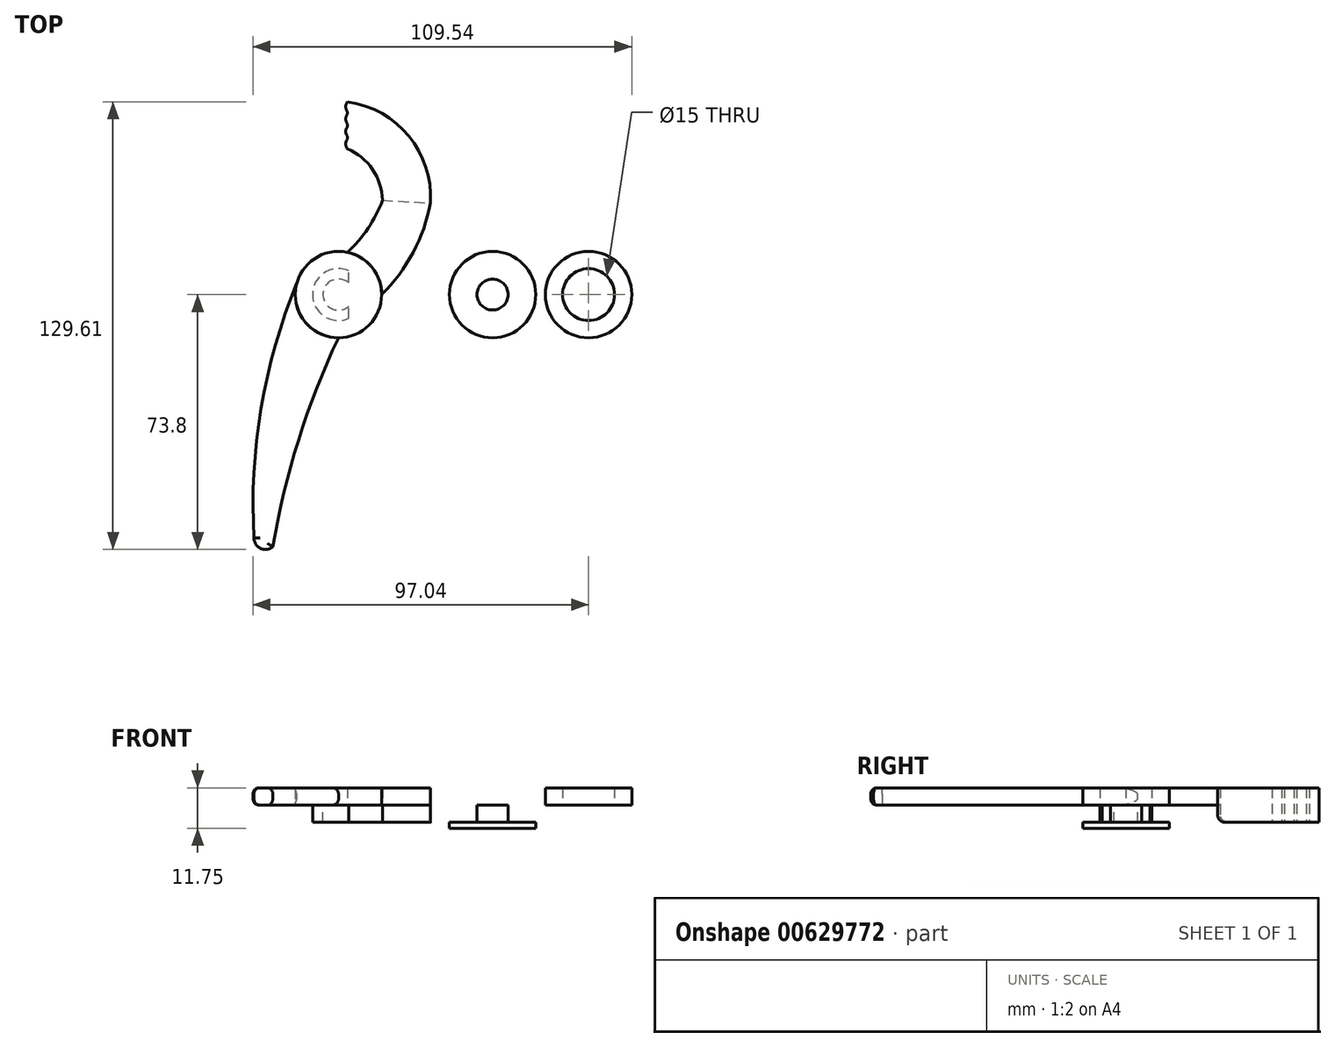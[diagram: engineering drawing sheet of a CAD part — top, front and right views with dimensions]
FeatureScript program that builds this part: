
annotation { "Feature Type Name" : "Feature", "Feature Type Description" : "" }
export const myFeature = defineFeature(function(context is Context, id is Id, definition is map)
    precondition{}
    {
        {
            var Q0;
            Q0=qCreatedBy(makeId("Top.planeOp"),FACE);
            var sketch = newSketch(context, id + "F0", { "sketchPlane" : qUnion([Q0])});
            skCircle(sketch, "E0", {"center": v(0, 0) * mm, "radius": 12.5 * mm});
            skArc(sketch, "E1", {"start": v(0, -12.5) * mm, "mid": v(-11.56, -42.1) * mm, "end": v(-19, -73) * mm});
            skArc(sketch, "E2", {"start": v(-24.43, -70.5) * mm, "mid": v(-22.51, -73.5) * mm, "end": v(-19, -73) * mm});
            skArc(sketch, "E3", {"start": v(-12.08, 3.22) * mm, "mid": v(-22.4, -32.95) * mm, "end": v(-24.43, -70.5) * mm});
            skArc(sketch, "E4", {"start": v(2.57, 12.23) * mm, "mid": v(8.53, 19.17) * mm, "end": v(12.73, 27.3) * mm});
            skArc(sketch, "E5", {"start": v(12.73, 27.3) * mm, "mid": v(9.86, 36.23) * mm, "end": v(2.65, 42.22) * mm});
            skLineSegment(sketch, "E6", {"start": v(2.65, 42.22) * mm, "end": v(2.65, 55.8) * mm});
            skArc(sketch, "E7", {"start": v(26.6, 26.5) * mm, "mid": v(20.35, 45.84) * mm, "end": v(2.65, 55.8) * mm});
            skArc(sketch, "E8", {"start": v(12.5, 0) * mm, "mid": v(21.58, 12.17) * mm, "end": v(26.6, 26.5) * mm});
            skLineSegment(sketch, "E9", {"start": v(12.73, 27.3) * mm, "end": v(26.6, 26.5) * mm});
            skSolve(sketch);
        }
        {
            var Q0;
            {var subQ0=sQuery(id+"F0.wireOp",EDGE,"E0");var subQ6=makeQuery(id+"F0.imprint","INTERSECT",VERTEX,{"derivedFrom":[subQ0,sQuery(id+"F0.wireOp",EDGE,"E4")]});Q0=makeQuery(id+"F0.imprint","IMPRINT",FACE,{"disambiguationData":[TD([[makeQuery(id+"F0.imprint","IMPRINT",EDGE,{"disambiguationData":[TD([[subQ6,1.0]])],"derivedFrom":subQ0}),1.0]])]});}
            extrude(context, id + "F1", {"entities" : qUnion([Q0]), "depth" : 5 * mm});
        }
        {
            var Q0;
            {var subQ0=sQuery(id+"F0.wireOp",EDGE,"E1");Q0=makeQuery(id+"F0.imprint","IMPRINT",FACE,{"disambiguationData":[TD([[makeQuery(id+"F0.imprint","IMPRINT",EDGE,{"derivedFrom":subQ0}),-1.0]])]});}
            var Q1;
            Q1=makeQuery(id+"F1.opExtrude","CAP_FACE",FACE,{"disambiguationData":[OSD([sQuery(id+"F0.wireOp",EDGE,"E0"),sQuery(id+"F0.wireOp",EDGE,"E3")])],"isStart":false});
            extrude(context, id + "F2", {"entities" : qUnion([Q0]), "endBound" : BoundingType.UP_TO_SURFACE, "endBoundEntityFace" : qUnion([Q1]), "depth" : 25 * mm});
        }
        {
            var Q0;
            {var subQ0=sQuery(id+"F0.wireOp",EDGE,"E4");Q0=makeQuery(id+"F0.imprint","IMPRINT",FACE,{"disambiguationData":[TD([[makeQuery(id+"F0.imprint","IMPRINT",EDGE,{"derivedFrom":subQ0}),-1.0]])]});}
            var Q1;
            Q1=makeQuery(id+"F1.opExtrude","CAP_FACE",FACE,{"disambiguationData":[OSD([sQuery(id+"F0.wireOp",EDGE,"E0"),sQuery(id+"F0.wireOp",EDGE,"E3")])],"isStart":false});
            extrude(context, id + "F3", {"entities" : qUnion([Q0]), "endBound" : BoundingType.UP_TO_SURFACE, "endBoundEntityFace" : qUnion([Q1]), "depth" : 25 * mm});
        }
        {
            var Q0;
            Q0=makeQuery(id+"F0.imprint","IMPRINT",FACE,{"disambiguationData":[TD([[makeQuery(id+"F0.imprint","IMPRINT",EDGE,{"derivedFrom":sQuery(id+"F0.wireOp",EDGE,"E5")}),-1.0]])]});
            var Q1;
            Q1=makeQuery(id+"F3.opExtrude","CAP_FACE",FACE,{"disambiguationData":[OSD([sQuery(id+"F0.wireOp",EDGE,"E0"),sQuery(id+"F0.wireOp",EDGE,"E4"),sQuery(id+"F0.wireOp",EDGE,"E8"),sQuery(id+"F0.wireOp",EDGE,"E9")])],"isStart":false});
            extrude(context, id + "F4", {"entities" : qUnion([Q0]), "operationType" : NewBodyOperationType.ADD, "endBound" : BoundingType.UP_TO_SURFACE, "endBoundEntityFace" : qUnion([Q1]), "depth" : 25 * mm, "hasSecondDirection" : true, "secondDirectionOppositeDirection" : true, "secondDirectionDepth" : 5 * mm});
        }
        {
            var Q0;
            Q0=qCreatedBy(makeId("Top.planeOp"),FACE);
            var sketch = newSketch(context, id + "F5", { "sketchPlane" : qUnion([Q0])});
            skCircle(sketch, "E10", {"center": v(0, 0) * mm, "radius": 7.5 * mm});
            skCircle(sketch, "E11.0", {"center": v(0, 0) * mm, "radius": 4.5 * mm});
            skLineSegment(sketch, "E12", {"start": v(0, 0) * mm, "end": v(0, 7.5) * mm});
            skLineSegment(sketch, "E13", {"start": v(-2.94, -6.9) * mm, "end": v(2.94, -6.9) * mm});
            skLineSegment(sketch, "E14", {"start": v(2.94, -6.9) * mm, "end": v(2.94, 6.9) * mm});
            skLineSegment(sketch, "E15", {"start": v(2.94, 6.9) * mm, "end": v(-2.94, 6.9) * mm});
            skLineSegment(sketch, "E16", {"start": v(-2.94, 6.9) * mm, "end": v(-2.94, -6.9) * mm});
            skSolve(sketch);
        }
        {
            var Q0;
            {var subQ0=sQuery(id+"F5.wireOp",EDGE,"E16");var subQ4=sQuery(id+"F5.wireOp",EDGE,"E11.0");var subQ5=makeQuery(id+"F5.imprint","INTERSECT",VERTEX,{"disambiguationData":[OD(0.0)],"derivedFrom":[subQ4,subQ0]});Q0=makeQuery(id+"F5.imprint","IMPRINT",FACE,{"disambiguationData":[TD([[makeQuery(id+"F5.imprint","IMPRINT",EDGE,{"disambiguationData":[TD([[subQ5,-1.0]])],"derivedFrom":subQ4}),-1.0]])]});}
            var Q1;
            {var subQ0=sQuery(id+"F5.wireOp",EDGE,"E14");var subQ4=sQuery(id+"F5.wireOp",EDGE,"E11.0");var subQ5=makeQuery(id+"F5.imprint","INTERSECT",VERTEX,{"disambiguationData":[OD(0.0)],"derivedFrom":[subQ4,subQ0]});Q1=makeQuery(id+"F5.imprint","IMPRINT",FACE,{"disambiguationData":[TD([[makeQuery(id+"F5.imprint","IMPRINT",EDGE,{"disambiguationData":[TD([[subQ5,1.0]])],"derivedFrom":subQ4}),-1.0]])]});}
            var Q2;
            {var subQ5=sQuery(id+"F5.wireOp",EDGE,"E13");Q2=makeQuery(id+"F5.imprint","IMPRINT",FACE,{"disambiguationData":[TD([[makeQuery(id+"F5.imprint","IMPRINT",EDGE,{"derivedFrom":subQ5}),1.0]])]});}
            var Q3;
            {var subQ0=sQuery(id+"F5.wireOp",EDGE,"E13");Q3=makeQuery(id+"F5.imprint","IMPRINT",FACE,{"disambiguationData":[TD([[makeQuery(id+"F5.imprint","IMPRINT",EDGE,{"derivedFrom":subQ0}),-1.0]])]});}
            var Q4;
            {var subQ0=sQuery(id+"F5.wireOp",EDGE,"E12");var subQ1=sQuery(id+"F5.wireOp",EDGE,"E11.0");var subQ2=makeQuery(id+"F5.imprint","INTERSECT",VERTEX,{"derivedFrom":[subQ1,subQ0]});Q4=makeQuery(id+"F5.imprint","IMPRINT",FACE,{"disambiguationData":[TD([[makeQuery(id+"F5.imprint","IMPRINT",EDGE,{"disambiguationData":[TD([[subQ2,-1.0]])],"derivedFrom":subQ1}),-1.0]])]});}
            var Q5;
            {var subQ0=sQuery(id+"F5.wireOp",EDGE,"E12");var subQ1=sQuery(id+"F5.wireOp",EDGE,"E11.0");var subQ2=makeQuery(id+"F5.imprint","INTERSECT",VERTEX,{"derivedFrom":[subQ1,subQ0]});Q5=makeQuery(id+"F5.imprint","IMPRINT",FACE,{"disambiguationData":[TD([[makeQuery(id+"F5.imprint","IMPRINT",EDGE,{"disambiguationData":[TD([[subQ2,1.0]])],"derivedFrom":subQ1}),-1.0]])]});}
            var Q6;
            {var subQ0=sQuery(id+"F5.wireOp",EDGE,"E12");var subQ1=sQuery(id+"F5.wireOp",EDGE,"E10");var subQ2=makeQuery(id+"F5.imprint","INTERSECT",VERTEX,{"derivedFrom":[subQ1,subQ0]});Q6=makeQuery(id+"F5.imprint","IMPRINT",FACE,{"disambiguationData":[TD([[makeQuery(id+"F5.imprint","IMPRINT",EDGE,{"disambiguationData":[TD([[subQ2,1.0]])],"derivedFrom":subQ0}),-1.0]])]});}
            var Q7;
            {var subQ0=sQuery(id+"F5.wireOp",EDGE,"E12");var subQ1=sQuery(id+"F5.wireOp",EDGE,"E10");var subQ2=makeQuery(id+"F5.imprint","INTERSECT",VERTEX,{"derivedFrom":[subQ1,subQ0]});Q7=makeQuery(id+"F5.imprint","IMPRINT",FACE,{"disambiguationData":[TD([[makeQuery(id+"F5.imprint","IMPRINT",EDGE,{"disambiguationData":[TD([[subQ2,1.0]])],"derivedFrom":subQ0}),1.0]])]});}
            extrude(context, id + "F6", {"entities" : qUnion([Q0, Q1, Q2, Q3, Q4, Q5, Q6, Q7]), "operationType" : NewBodyOperationType.ADD, "oppositeDirection" : true, "depth" : 5 * mm});
        }
        {
            var Q0;
            Q0=qCreatedBy(makeId("Top.planeOp"),FACE);
            var sketch = newSketch(context, id + "F7", { "sketchPlane" : qUnion([Q0])});
            skCircle(sketch, "E17", {"center": v(72.33, 0) * mm, "radius": 12.5 * mm});
            skCircle(sketch, "E18", {"center": v(72.33, 0) * mm, "radius": 7.5 * mm});
            skCircle(sketch, "E19", {"center": v(44.58, 0) * mm, "radius": 4.49 * mm});
            skSolve(sketch);
        }
        {
            var Q0;
            Q0=makeQuery(id+"F7.imprint","IMPRINT",FACE,{"disambiguationData":[TD([[makeQuery(id+"F7.imprint","IMPRINT",EDGE,{"derivedFrom":sQuery(id+"F7.wireOp",EDGE,"E17")}),1.0]])]});
            extrude(context, id + "F8", {"entities" : qUnion([Q0]), "depth" : 5 * mm});
        }
        {
            var Q0;
            Q0=makeQuery(id+"F7.imprint","IMPRINT",FACE,{"disambiguationData":[TD([[makeQuery(id+"F7.imprint","IMPRINT",EDGE,{"derivedFrom":sQuery(id+"F7.wireOp",EDGE,"E19")}),1.0]])]});
            extrude(context, id + "F9", {"entities" : qUnion([Q0]), "oppositeDirection" : true, "depth" : 5 * mm});
        }
        {
            var Q0;
            Q0=makeQuery(id+"F9.opExtrude","CAP_FACE",FACE,{"disambiguationData":[OSD([sQuery(id+"F7.wireOp",EDGE,"E19")])],"isStart":false});
            var sketch = newSketch(context, id + "F10", { "sketchPlane" : qUnion([Q0])});
            skCircle(sketch, "E20", {"center": v(44.58, 0) * mm, "radius": 12.5 * mm});
            skSolve(sketch);
        }
        {
            var Q0;
            Q0=makeQuery(id+"F10.imprint","IMPRINT",FACE,{"disambiguationData":[TD([[makeQuery(id+"F10.imprint","IMPRINT",EDGE,{"derivedFrom":sQuery(id+"F10.wireOp",EDGE,"E20")}),1.0]])]});
            var Q1;
            Q1=makeQuery(id+"F10.imprint","IMPRINT",FACE,{"disambiguationData":[TD([[makeQuery(id+"F10.imprint","IMPRINT",EDGE,{"derivedFrom":makeQuery(id+"F9.opExtrude","CAP_EDGE",EDGE,{"disambiguationData":[OSD([sQuery(id+"F7.wireOp",EDGE,"E19")])],"isStart":false})}),-1.0]])]});
            extrude(context, id + "F11", {"entities" : qUnion([Q0, Q1]), "operationType" : NewBodyOperationType.ADD, "depth" : 1.75 * mm});
        }
        {
            var Q0;
            Q0=makeQuery(id+"F2.opExtrude","CAP_EDGE",EDGE,{"disambiguationData":[OSD([sQuery(id+"F0.wireOp",EDGE,"E1")])],"isStart":true});
            var Q1;
            Q1=makeQuery(id+"F2.opExtrude","CAP_EDGE",EDGE,{"disambiguationData":[OSD([sQuery(id+"F0.wireOp",EDGE,"E1")])],"isStart":false});
            var Q2;
            Q2=makeQuery(id+"F2.opExtrude","CAP_EDGE",EDGE,{"disambiguationData":[OSD([sQuery(id+"F0.wireOp",EDGE,"E3")])],"isStart":true});
            var Q3;
            Q3=makeQuery(id+"F2.opExtrude","CAP_EDGE",EDGE,{"disambiguationData":[OSD([sQuery(id+"F0.wireOp",EDGE,"E3")])],"isStart":false});
            var Q4;
            Q4=makeQuery(id+"F2.opExtrude","CAP_EDGE",EDGE,{"disambiguationData":[OSD([sQuery(id+"F0.wireOp",EDGE,"E2")])],"isStart":false});
            var Q5;
            Q5=makeQuery(id+"F2.opExtrude","CAP_EDGE",EDGE,{"disambiguationData":[OSD([sQuery(id+"F0.wireOp",EDGE,"E2")])],"isStart":true});
            fillet(context, id + "F12", {"entities" : qUnion([Q0, Q1, Q2, Q3, Q4, Q5]), "radius" : 1.69 * mm, "tangentPropagation" : true, "allowEdgeOverflow" : false});
        }
        {
            var Q0;
            Q0=makeQuery(id+"F4.opExtrude","CAP_FACE",FACE,{"disambiguationData":[OSD([sQuery(id+"F0.wireOp",EDGE,"E5"),sQuery(id+"F0.wireOp",EDGE,"E6"),sQuery(id+"F0.wireOp",EDGE,"E7"),sQuery(id+"F0.wireOp",EDGE,"E9")])],"isStart":true});
            var sketch = newSketch(context, id + "F13", { "sketchPlane" : qUnion([Q0])});
            skArc(sketch, "E21", {"start": v(2.65, -53.01) * mm, "mid": v(2.08, -54.4) * mm, "end": v(2.65, -55.8) * mm});
            skArc(sketch, "E22.1.0.0", {"start": v(2.65, -49.41) * mm, "mid": v(2.08, -50.81) * mm, "end": v(2.65, -52.2) * mm});
            skArc(sketch, "E22.2.0.0", {"start": v(2.65, -45.82) * mm, "mid": v(2.08, -47.21) * mm, "end": v(2.65, -48.61) * mm});
            skArc(sketch, "E22.3.0.0", {"start": v(2.65, -42.22) * mm, "mid": v(2.08, -43.62) * mm, "end": v(2.65, -45.02) * mm});
            skLineSegment(sketch, "E22.direction1", {"start": v(2.65, -55.8) * mm, "end": v(2.65, -52.2) * mm, "construction": true});
            skLineSegment(sketch, "E23", {"start": v(2.65, -52.2) * mm, "end": v(2.65, -49.41) * mm});
            skLineSegment(sketch, "E24", {"start": v(2.65, -48.61) * mm, "end": v(2.65, -45.82) * mm});
            skSolve(sketch);
        }
        {
            var Q0;
            {var subQ0=sQuery(id+"F13.wireOp",EDGE,"E21");Q0=makeQuery(id+"F13.imprint","IMPRINT",FACE,{"disambiguationData":[TD([[makeQuery(id+"F13.imprint","IMPRINT",EDGE,{"derivedFrom":subQ0}),1.0]])]});}
            var Q1;
            Q1=makeQuery(id+"F13.imprint","IMPRINT",FACE,{"disambiguationData":[TD([[makeQuery(id+"F13.imprint","IMPRINT",EDGE,{"derivedFrom":sQuery(id+"F13.wireOp",EDGE,"E22.1.0.0")}),1.0]])]});
            var Q2;
            Q2=makeQuery(id+"F13.imprint","IMPRINT",FACE,{"disambiguationData":[TD([[makeQuery(id+"F13.imprint","IMPRINT",EDGE,{"derivedFrom":sQuery(id+"F13.wireOp",EDGE,"E22.2.0.0")}),1.0]])]});
            var Q3;
            {var subQ0=sQuery(id+"F13.wireOp",EDGE,"E22.3.0.0");Q3=makeQuery(id+"F13.imprint","IMPRINT",FACE,{"disambiguationData":[TD([[makeQuery(id+"F13.imprint","IMPRINT",EDGE,{"derivedFrom":subQ0}),1.0]])]});}
            var Q4;
            {var subQ0=sQuery(id+"F0.wireOp",EDGE,"E9");Q4=makeQuery(id+"F4.boolean.opBoolean","MERGE",FACE,{"derivedFrom":[makeQuery(id+"F3.opExtrude","CAP_FACE",FACE,{"disambiguationData":[OSD([sQuery(id+"F0.wireOp",EDGE,"E0"),sQuery(id+"F0.wireOp",EDGE,"E4"),sQuery(id+"F0.wireOp",EDGE,"E8"),subQ0])],"isStart":false}),makeQuery(id+"F4.opExtrude","CAP_FACE",FACE,{"disambiguationData":[OSD([sQuery(id+"F0.wireOp",EDGE,"E5"),sQuery(id+"F0.wireOp",EDGE,"E6"),sQuery(id+"F0.wireOp",EDGE,"E7"),subQ0])],"isStart":false})]});}
            extrude(context, id + "F14", {"entities" : qUnion([Q0, Q1, Q2, Q3]), "operationType" : NewBodyOperationType.ADD, "endBound" : BoundingType.UP_TO_SURFACE, "oppositeDirection" : true, "endBoundEntityFace" : qUnion([Q4]), "depth" : 25 * mm});
        }
        {
            var Q0;
            Q0=makeQuery(id+"F4.opExtrude","CAP_EDGE",EDGE,{"disambiguationData":[OSD([sQuery(id+"F0.wireOp",EDGE,"E9")])],"isStart":true});
            fillet(context, id + "F15", {"entities" : qUnion([Q0]), "radius" : 2.17 * mm, "tangentPropagation" : true, "allowEdgeOverflow" : false});
        }
    });
